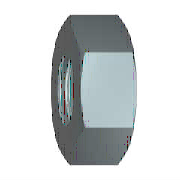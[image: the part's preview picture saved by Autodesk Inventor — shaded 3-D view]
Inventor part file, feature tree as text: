
AUTODESK INVENTOR PART (.ipt)
format: ipt  version: 2020 (Build 240168000, 168)  size: 164,352 bytes
history: native  units: mm (DEFAULTED — no unit token found)
features: sketch x3, chamfer x1, hole x1, other x1, plane x1
ambient origin geometry x7: Origin, YZ Plane, XZ Plane, X Axis, Y Axis, Z Axis, Center Point
bodies: Solid1 (feature_tree), Body (feature_tree)
feature tree (7):
  chamfer  "Chamfer1"  Angle=30.0deg  [1 undecoded]
  hole  "Thread"  [1 undecoded]
  other  "Work Axis1"
  plane  "Work Plane1"
  sketch  "Sketch1"  dims[d0=9.237604mm]
  sketch  "Sketch2"  dims[d1=4.0mm]
  sketch  "Sketch3"  dims[d2=0.0mm d3=30.0deg d4=30.0deg d5=6.8mm d6=6.8mm d7=90.0deg d25=4.134mm d26=6.0mm d27=4.0mm d28=2.0mm d29=14.3117mm d30=8.0mm d31=20.594885mm d8=0.433013mm d9=30.0deg d10=0.433013mm d11=30.0deg d13=0.0mm d14=0.0mm d39=0.0mm d40=0.433013mm d41=0.433013mm d42=0.0mm]
note: 2 required parameter values undecoded (feature->parameter linkage not recoverable at this tier; creation-order binding heuristic only, values carry confidence <= 0.55)
